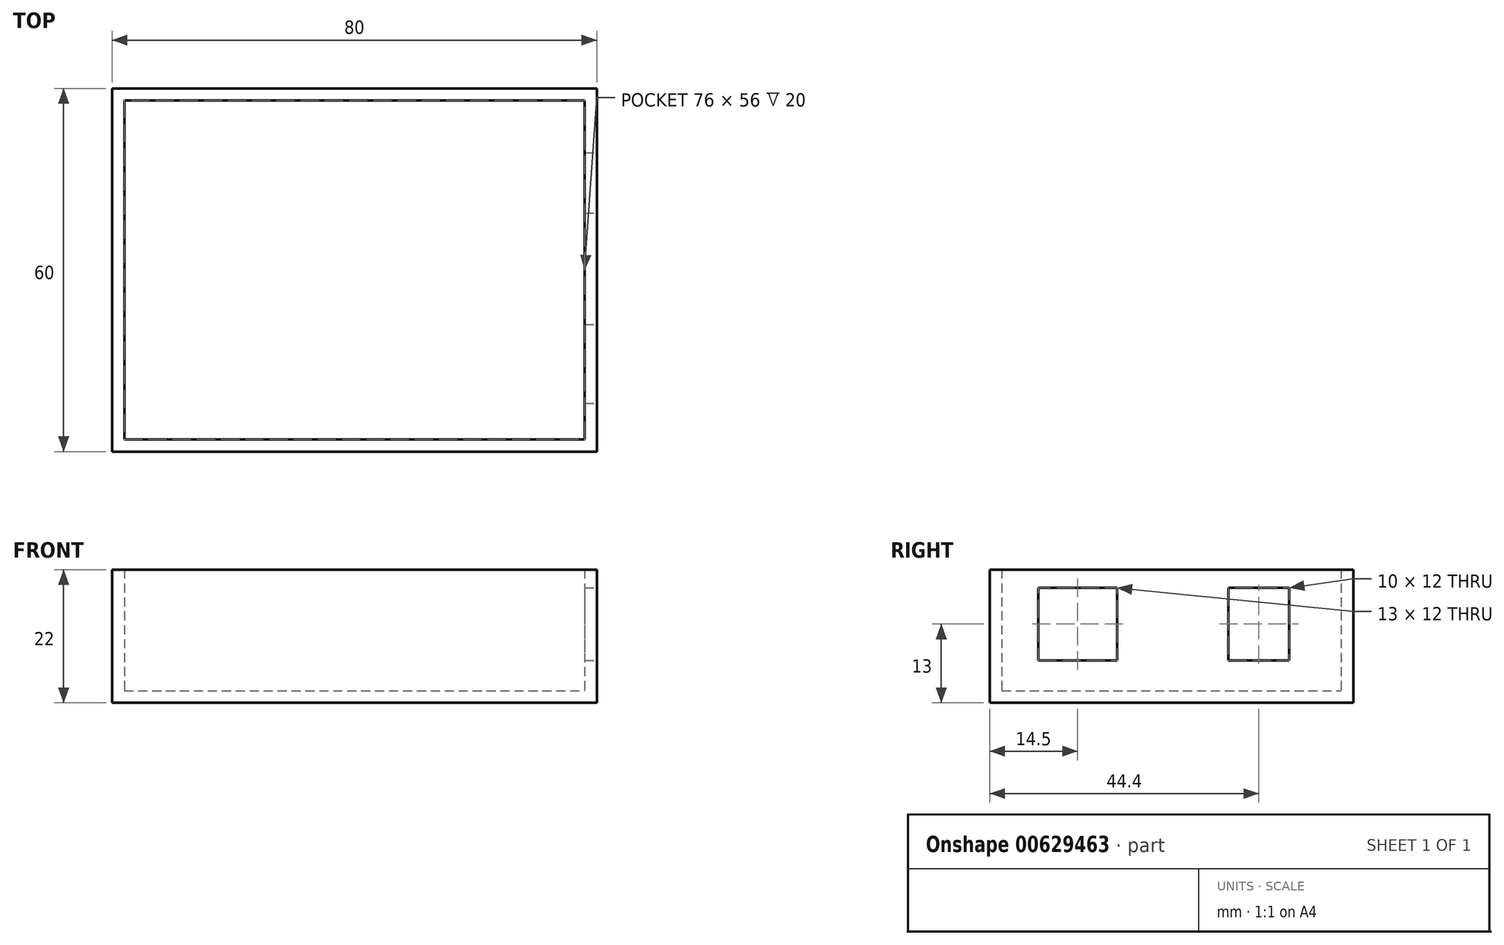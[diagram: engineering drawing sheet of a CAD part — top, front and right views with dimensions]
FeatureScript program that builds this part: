
annotation { "Feature Type Name" : "Feature", "Feature Type Description" : "" }
export const myFeature = defineFeature(function(context is Context, id is Id, definition is map)
    precondition{}
    {
        {
            var Q0;
            Q0=qCreatedBy(makeId("Top.planeOp"),FACE);
            var sketch = newSketch(context, id + "F0", { "sketchPlane" : qUnion([Q0])});
            skLineSegment(sketch, "E0.bottom", {"start": v(40, -30) * mm, "end": v(-40, -30) * mm});
            skLineSegment(sketch, "E0.top", {"start": v(40, 30) * mm, "end": v(-40, 30) * mm});
            skLineSegment(sketch, "E0.left", {"start": v(40, -30) * mm, "end": v(40, 30) * mm});
            skLineSegment(sketch, "E0.right", {"start": v(-40, -30) * mm, "end": v(-40, 30) * mm});
            skPoint(sketch, "E0.middle", {"position": v(0, 0) * mm});
            skSolve(sketch);
        }
        {
            var Q0;
            Q0 = qSketchRegion(id + "F0", true);
            extrude(context, id + "F1", {"entities" : qUnion([Q0]), "depth" : 2 * mm, "offsetDistance" : 25 * mm});
        }
        {
            var Q0;
            Q0=makeQuery(id+"F1.opExtrude","CAP_FACE",FACE,{"disambiguationData":[OSD([sQuery(id+"F0.wireOp",EDGE,"E0.bottom"),sQuery(id+"F0.wireOp",EDGE,"E0.top"),sQuery(id+"F0.wireOp",EDGE,"E0.left"),sQuery(id+"F0.wireOp",EDGE,"E0.right")])],"isStart":false});
            var sketch = newSketch(context, id + "F2", { "sketchPlane" : qUnion([Q0])});
            skLineSegment(sketch, "E1.bottom", {"start": v(-40, -30) * mm, "end": v(40, -30) * mm});
            skLineSegment(sketch, "E1.top", {"start": v(-40, 30) * mm, "end": v(40, 30) * mm});
            skLineSegment(sketch, "E1.left", {"start": v(-40, -30) * mm, "end": v(-40, 30) * mm});
            skLineSegment(sketch, "E1.right", {"start": v(40, -30) * mm, "end": v(40, 30) * mm});
            skPoint(sketch, "E1.middle", {"position": v(0, 0) * mm});
            skLineSegment(sketch, "E2.bottom", {"start": v(-38, -28) * mm, "end": v(38, -28) * mm});
            skLineSegment(sketch, "E2.top", {"start": v(-38, 28) * mm, "end": v(38, 28) * mm});
            skLineSegment(sketch, "E2.left", {"start": v(-38, -28) * mm, "end": v(-38, 28) * mm});
            skLineSegment(sketch, "E2.right", {"start": v(38, -28) * mm, "end": v(38, 28) * mm});
            skSolve(sketch);
        }
        {
            var Q0;
            Q0 = qSketchRegion(id + "F2", true);
            extrude(context, id + "F3", {"entities" : qUnion([Q0]), "operationType" : NewBodyOperationType.ADD, "depth" : 20 * mm, "offsetDistance" : 25 * mm});
        }
        {
            var Q0;
            Q0=makeQuery(id+"F3.boolean.opBoolean","MERGE",FACE,{"derivedFrom":[makeQuery(id+"F1.opExtrude","SWEPT_FACE",FACE,{"disambiguationData":[OSD([sQuery(id+"F0.wireOp",EDGE,"E0.left")])]}),makeQuery(id+"F3.opExtrude","SWEPT_FACE",FACE,{"disambiguationData":[OSD([sQuery(id+"F2.wireOp",EDGE,"E1.right")])]})]});
            var sketch = newSketch(context, id + "F4", { "sketchPlane" : qUnion([Q0])});
            skLineSegment(sketch, "E3.bottom", {"start": v(-22, 19) * mm, "end": v(-9, 19) * mm});
            skLineSegment(sketch, "E3.top", {"start": v(-22, 7) * mm, "end": v(-9, 7) * mm});
            skLineSegment(sketch, "E3.left", {"start": v(-22, 19) * mm, "end": v(-22, 7) * mm});
            skLineSegment(sketch, "E3.right", {"start": v(-9, 19) * mm, "end": v(-9, 7) * mm});
            skLineSegment(sketch, "E4.bottom", {"start": v(9.4, 19) * mm, "end": v(19.4, 19) * mm});
            skLineSegment(sketch, "E4.top", {"start": v(9.4, 7) * mm, "end": v(19.4, 7) * mm});
            skLineSegment(sketch, "E4.left", {"start": v(9.4, 19) * mm, "end": v(9.4, 7) * mm});
            skLineSegment(sketch, "E4.right", {"start": v(19.4, 19) * mm, "end": v(19.4, 7) * mm});
            skSolve(sketch);
        }
        {
            var Q0;
            Q0=makeQuery(id+"F4.imprint","IMPRINT",FACE,{"disambiguationData":[TD([[makeQuery(id+"F4.imprint","IMPRINT",EDGE,{"derivedFrom":sQuery(id+"F4.wireOp",EDGE,"E3.bottom")}),-1.0]])]});
            var Q1;
            Q1=makeQuery(id+"F4.imprint","IMPRINT",FACE,{"disambiguationData":[TD([[makeQuery(id+"F4.imprint","IMPRINT",EDGE,{"derivedFrom":sQuery(id+"F4.wireOp",EDGE,"E4.bottom")}),-1.0]])]});
            extrude(context, id + "F5", {"entities" : qUnion([Q0, Q1]), "operationType" : NewBodyOperationType.REMOVE, "oppositeDirection" : true, "depth" : 2 * mm, "offsetDistance" : 25 * mm});
        }
        {
            var Q0;
            Q0=makeQuery(id+"F1.opExtrude","CAP_FACE",FACE,{"disambiguationData":[OSD([sQuery(id+"F0.wireOp",EDGE,"E0.bottom"),sQuery(id+"F0.wireOp",EDGE,"E0.top"),sQuery(id+"F0.wireOp",EDGE,"E0.left"),sQuery(id+"F0.wireOp",EDGE,"E0.right")])],"isStart":false});
            var sketch = newSketch(context, id + "F6", { "sketchPlane" : qUnion([Q0])});
            skCircle(sketch, "E5", {"center": v(-27.99, 12.97) * mm, "radius": 3.75 * mm});
            skCircle(sketch, "E6", {"center": v(12.97, 14.33) * mm, "radius": 3.75 * mm});
            skCircle(sketch, "E7", {"center": v(24.5, -15.25) * mm, "radius": 3.75 * mm});
            skCircle(sketch, "E8", {"center": v(-27.08, -9.33) * mm, "radius": 3.75 * mm});
            skSolve(sketch);
        }
        {
            var Q0;
            Q0=sQuery(id+"F6.wireOp",EDGE,"E7");
            var Q1;
            Q1=sQuery(id+"F6.wireOp",EDGE,"E6");
            var Q2;
            Q2=sQuery(id+"F6.wireOp",EDGE,"E5");
            var Q3;
            Q3=sQuery(id+"F6.wireOp",EDGE,"E8");
            extrude(context, id + "F7", {"bodyType" : ToolBodyType.SURFACE, "surfaceEntities" : qUnion([Q0, Q1, Q2, Q3]), "depth" : 10 * mm, "offsetDistance" : 25 * mm});
        }
    });
